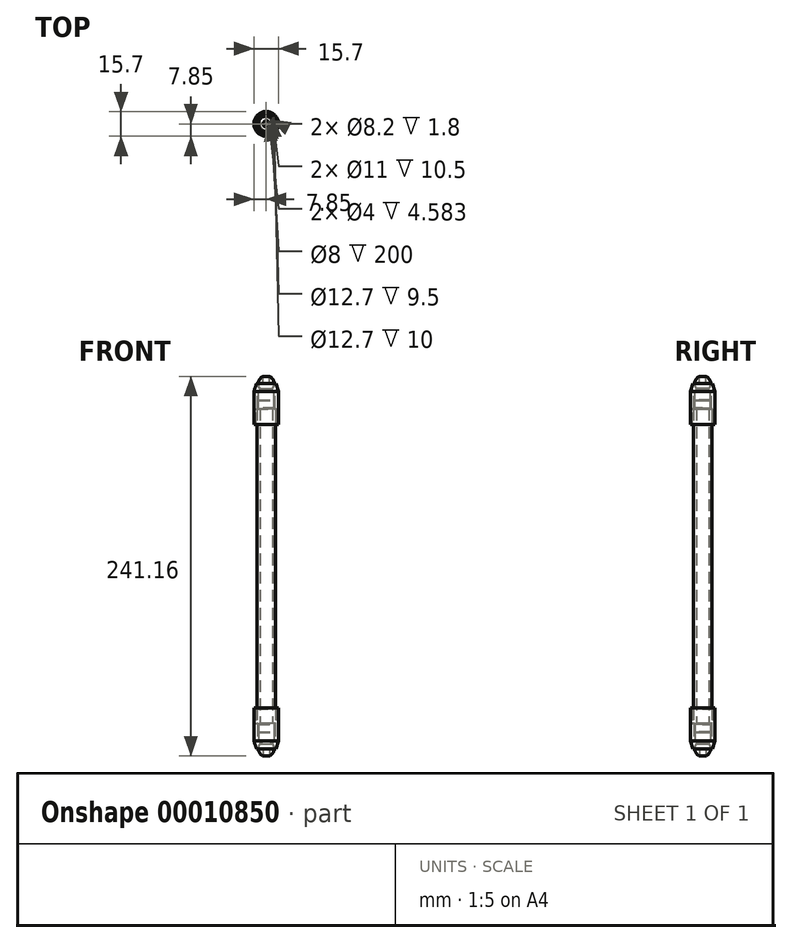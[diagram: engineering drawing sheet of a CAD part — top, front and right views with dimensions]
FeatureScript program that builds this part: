
annotation { "Feature Type Name" : "Feature", "Feature Type Description" : "" }
export const myFeature = defineFeature(function(context is Context, id is Id, definition is map)
    precondition{}
    {
        {
            var Q0;
            Q0=qCreatedBy(makeId("Front.planeOp"),FACE);
            var sketch = newSketch(context, id + "F0", { "sketchPlane" : qUnion([Q0])});
            skArc(sketch, "E0", {"start": v(-4.1, 3.2) * mm, "mid": v(-4.92, 1.7) * mm, "end": v(-5.2, 0) * mm});
            skLineSegment(sketch, "E1", {"start": v(-5.2, 0) * mm, "end": v(-6.2, 0) * mm});
            skLineSegment(sketch, "E2", {"start": v(-7.85, 5) * mm, "end": v(-7.85, 26) * mm});
            skLineSegment(sketch, "E3", {"start": v(-7.85, 26) * mm, "end": v(-6.35, 26) * mm});
            skLineSegment(sketch, "E4", {"start": v(-6.35, 26) * mm, "end": v(-6.35, 16) * mm});
            skLineSegment(sketch, "E5", {"start": v(-6.35, 16) * mm, "end": v(-5.5, 16) * mm});
            skLineSegment(sketch, "E6", {"start": v(-5.5, 16) * mm, "end": v(-5.5, 5) * mm});
            skLineSegment(sketch, "E7", {"start": v(-5.5, 5) * mm, "end": v(-4.1, 5) * mm});
            skLineSegment(sketch, "E8", {"start": v(0, 5.2) * mm, "end": v(0, 5) * mm});
            skLineSegment(sketch, "E9", {"start": v(-6.2, 0) * mm, "end": v(-7.85, 5) * mm});
            skLineSegment(sketch, "E10", {"start": v(0, 0) * mm, "end": v(0, 32.36) * mm, "construction": true});
            skLineSegment(sketch, "E11", {"start": v(2.85, 3.2) * mm, "end": v(-9.79, 3.2) * mm, "construction": true});
            skLineSegment(sketch, "E12", {"start": v(-4.1, 3.2) * mm, "end": v(-4.1, 5) * mm});
            skCircle(sketch, "E13", {"center": v(0, 0) * mm, "radius": 5 * mm});
            skLineSegment(sketch, "E14", {"start": v(0, 5) * mm, "end": v(0, -5) * mm});
            skLineSegment(sketch, "E15", {"start": v(0, 15.75) * mm, "end": v(-5, 15.75) * mm});
            skLineSegment(sketch, "E16", {"start": v(-5, 15.75) * mm, "end": v(-5, 10.75) * mm});
            skLineSegment(sketch, "E17", {"start": v(-5, 10.75) * mm, "end": v(0, 10.75) * mm});
            skLineSegment(sketch, "E18", {"start": v(0, 10.75) * mm, "end": v(0, 15.75) * mm});
            skLineSegment(sketch, "E19", {"start": v(0, 5.5) * mm, "end": v(-5, 5.5) * mm});
            skLineSegment(sketch, "E20", {"start": v(-5, 5.5) * mm, "end": v(-5, 10.5) * mm});
            skLineSegment(sketch, "E21", {"start": v(-5, 10.5) * mm, "end": v(0, 10.5) * mm});
            skLineSegment(sketch, "E22", {"start": v(0, 10.5) * mm, "end": v(0, 5.5) * mm});
            skLineSegment(sketch, "E23", {"start": v(-4, 3) * mm, "end": v(4, 3) * mm, "construction": true});
            skSolve(sketch);
        }
        {
            var Q0;
            Q0=makeQuery(id+"F0.imprint","IMPRINT",FACE,{"disambiguationData":[TD([[makeQuery(id+"F0.imprint","IMPRINT",EDGE,{"derivedFrom":sQuery(id+"F0.wireOp",EDGE,"E0")}),-1.0]])]});
            var Q1;
            {var subQ0=sQuery(id+"F0.wireOp",EDGE,"E14");Q1=makeQuery(id+"F0.imprint","IMPRINT",FACE,{"disambiguationData":[TD([[makeQuery(id+"F0.imprint","IMPRINT",EDGE,{"derivedFrom":subQ0}),-1.0]])]});}
            var Q2;
            Q2=makeQuery(id+"F0.imprint","IMPRINT",FACE,{"disambiguationData":[TD([[makeQuery(id+"F0.imprint","IMPRINT",EDGE,{"derivedFrom":sQuery(id+"F0.wireOp",EDGE,"E19")}),-1.0]])]});
            var Q3;
            Q3=makeQuery(id+"F0.imprint","IMPRINT",FACE,{"disambiguationData":[TD([[makeQuery(id+"F0.imprint","IMPRINT",EDGE,{"derivedFrom":sQuery(id+"F0.wireOp",EDGE,"E15")}),1.0]])]});
            var Q4;
            Q4=sQuery(id+"F0.wireOp",EDGE,"E10");
            revolve(context, id + "F1", {"entities" : qUnion([Q0, Q1, Q2, Q3]), "axis" : qUnion([Q4]), "revolveType" : RevolveType.FULL});
        }
        {
            var Q0;
            Q0=makeQuery(id+"F1.opRevolve","SWEPT_EDGE",EDGE,{"disambiguationData":[OSD([sQuery(id+"F0.wireOp",EDGE,"E5"),sQuery(id+"F0.wireOp",EDGE,"E6")])]});
            chamfer(context, id + "F2", {"entities" : qUnion([Q0]), "width" : 0.5 * mm, "tangentPropagation" : true});
        }
        {
            var Q0;
            Q0=makeQuery(id+"F1.opRevolve","SWEPT_FACE",FACE,{"disambiguationData":[OSD([sQuery(id+"F0.wireOp",EDGE,"E5")])]});
            var sketch = newSketch(context, id + "F3", { "sketchPlane" : qUnion([Q0])});
            skCircle(sketch, "E24", {"center": v(0, 0) * mm, "radius": 6 * mm});
            skCircle(sketch, "E25", {"center": v(0, 0) * mm, "radius": 4 * mm});
            skSolve(sketch);
        }
        {
            var Q0;
            Q0=makeQuery(id+"F3.imprint","IMPRINT",FACE,{"disambiguationData":[TD([[makeQuery(id+"F3.imprint","IMPRINT",EDGE,{"derivedFrom":sQuery(id+"F3.wireOp",EDGE,"E25")}),-1.0]])]});
            extrude(context, id + "F4", {"entities" : qUnion([Q0]), "depth" : 200 * mm});
        }
        {
            var Q0;
            Q0=makeQuery(id+"F4.opExtrude","CAP_FACE",FACE,{"disambiguationData":[OSD([sQuery(id+"F0.wireOp",EDGE,"E5"),sQuery(id+"F0.wireOp",EDGE,"E6"),sQuery(id+"F3.wireOp",EDGE,"E25")])],"isStart":false});
            cPlane(context, id + "F5", {"entities" : qUnion([Q0]), "cplaneType" : CPlaneType.OFFSET, "offset" : 100 * mm, "oppositeDirection" : true, "width" : 150 * mm, "height" : 150 * mm});
        }
        {
            var Q0;
            Q0=qCreatedBy(makeId("Top.planeOp"),FACE);
            cPlane(context, id + "F6", {"entities" : qUnion([Q0]), "cplaneType" : CPlaneType.OFFSET, "offset" : 5 * mm, "oppositeDirection" : true, "width" : 150 * mm, "height" : 150 * mm});
        }
        {
            var Q0;
            Q0=qCreatedBy(id+"F6.planeOp",FACE);
            var sketch = newSketch(context, id + "F7", { "sketchPlane" : qUnion([Q0])});
            skCircle(sketch, "E26", {"center": v(0, 0) * mm, "radius": 2 * mm});
            skSolve(sketch);
        }
        {
            var Q0;
            Q0=makeQuery(id+"F7.imprint","IMPRINT",FACE,{"disambiguationData":[TD([[makeQuery(id+"F7.imprint","IMPRINT",EDGE,{"derivedFrom":sQuery(id+"F7.wireOp",EDGE,"E26")}),1.0]])]});
            extrude(context, id + "F8", {"entities" : qUnion([Q0]), "operationType" : NewBodyOperationType.REMOVE, "depth" : 5 * mm});
        }
        {
            var Q0;
            Q0=makeQuery(id+"F1.opRevolve","SWEPT_BODY",BODY,{"disambiguationData":[OSD([sQuery(id+"F0.wireOp",EDGE,"E19"),sQuery(id+"F0.wireOp",EDGE,"E20"),sQuery(id+"F0.wireOp",EDGE,"E21"),sQuery(id+"F0.wireOp",EDGE,"E22")])]});
            var Q1;
            Q1=makeQuery(id+"F1.opRevolve","SWEPT_BODY",BODY,{"disambiguationData":[OSD([sQuery(id+"F0.wireOp",EDGE,"E15"),sQuery(id+"F0.wireOp",EDGE,"E16"),sQuery(id+"F0.wireOp",EDGE,"E17"),sQuery(id+"F0.wireOp",EDGE,"E18")])]});
            var Q2;
            Q2=makeQuery(id+"F1.opRevolve","SWEPT_BODY",BODY,{"disambiguationData":[OSD([sQuery(id+"F0.wireOp",EDGE,"E13"),sQuery(id+"F0.wireOp",EDGE,"E14")])]});
            var Q3;
            Q3=makeQuery(id+"F1.opRevolve","SWEPT_BODY",BODY,{"disambiguationData":[OSD([sQuery(id+"F0.wireOp",EDGE,"E0"),sQuery(id+"F0.wireOp",EDGE,"E1"),sQuery(id+"F0.wireOp",EDGE,"E2"),sQuery(id+"F0.wireOp",EDGE,"E3"),sQuery(id+"F0.wireOp",EDGE,"E4"),sQuery(id+"F0.wireOp",EDGE,"E5"),sQuery(id+"F0.wireOp",EDGE,"E6"),sQuery(id+"F0.wireOp",EDGE,"E7"),sQuery(id+"F0.wireOp",EDGE,"E9"),sQuery(id+"F0.wireOp",EDGE,"E12")])]});
            var Q4;
            Q4=qCreatedBy(id+"F5.planeOp",FACE);
            mirror(context, id + "F9", {"entities" : qUnion([Q0, Q1, Q2, Q3]), "mirrorPlane" : qUnion([Q4])});
        }
        {
            var Q0;
            Q0=makeQuery(id+"F1.opRevolve","SWEPT_EDGE",EDGE,{"disambiguationData":[OSD([sQuery(id+"F0.wireOp",EDGE,"E3"),sQuery(id+"F0.wireOp",EDGE,"E4")])]});
            var Q1;
            Q1=makeQuery(id+"F1.opRevolve","SWEPT_EDGE",EDGE,{"disambiguationData":[OSD([sQuery(id+"F0.wireOp",EDGE,"E3"),sQuery(id+"F0.wireOp",EDGE,"E4")])]});
            chamfer(context, id + "F10", {"entities" : qUnion([Q0, Q1]), "width" : 0.5 * mm, "tangentPropagation" : true});
        }
    });
